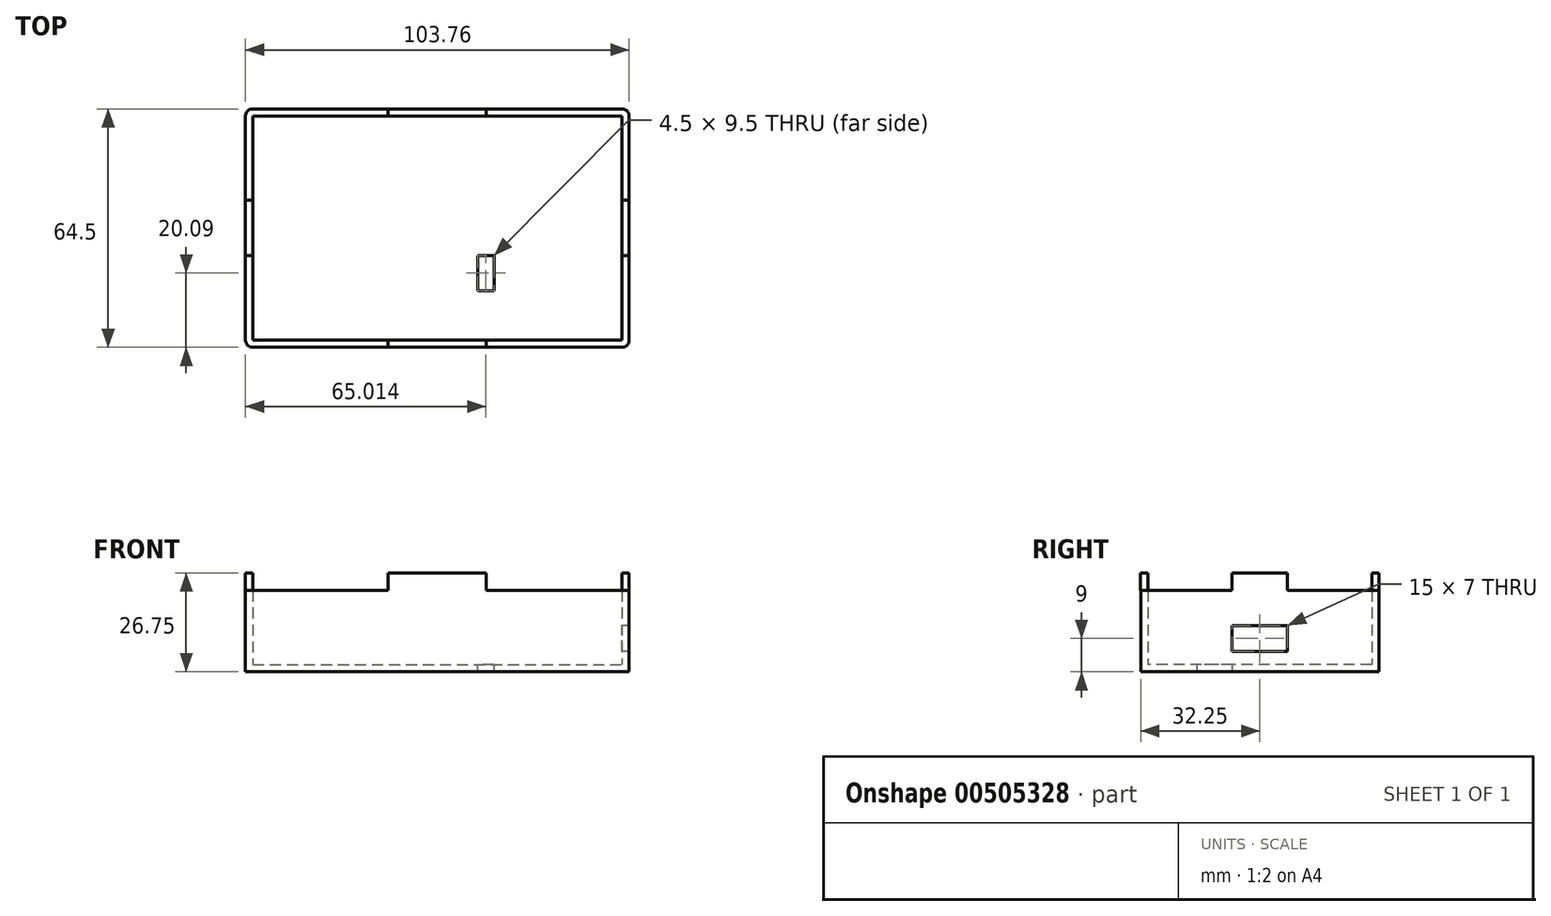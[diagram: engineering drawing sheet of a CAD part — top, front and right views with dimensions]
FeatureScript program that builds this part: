
annotation { "Feature Type Name" : "Feature", "Feature Type Description" : "" }
export const myFeature = defineFeature(function(context is Context, id is Id, definition is map)
    precondition{}
    {
        {
            var Q0;
            Q0=qCreatedBy(makeId("Top.planeOp"),FACE);
            var sketch = newSketch(context, id + "F0", { "sketchPlane" : qUnion([Q0])});
            skLineSegment(sketch, "E0.bottom", {"start": v(-51.88, 32.25) * mm, "end": v(51.88, 32.25) * mm});
            skLineSegment(sketch, "E0.top", {"start": v(-51.88, -32.25) * mm, "end": v(51.88, -32.25) * mm});
            skLineSegment(sketch, "E0.left", {"start": v(-51.88, 32.25) * mm, "end": v(-51.88, -32.25) * mm});
            skLineSegment(sketch, "E0.right", {"start": v(51.88, 32.25) * mm, "end": v(51.88, -32.25) * mm});
            skPoint(sketch, "E0.middle", {"position": v(0, 0) * mm});
            skPoint(sketch, "E1", {"position": v(-51.88, 0) * mm});
            skSolve(sketch);
        }
        {
            var Q0;
            Q0=makeQuery(id+"F0.imprint","IMPRINT",FACE,{"disambiguationData":[TD([[makeQuery(id+"F0.imprint","IMPRINT",EDGE,{"derivedFrom":sQuery(id+"F0.wireOp",EDGE,"E0.bottom")}),-1.0]])]});
            extrude(context, id + "F1", {"entities" : qUnion([Q0]), "depth" : 22 * mm});
        }
        {
            var Q0;
            Q0=makeQuery(id+"F1.opExtrude","CAP_FACE",FACE,{"disambiguationData":[OSD([sQuery(id+"F0.wireOp",EDGE,"E0.bottom"),sQuery(id+"F0.wireOp",EDGE,"E0.top"),sQuery(id+"F0.wireOp",EDGE,"E0.left"),sQuery(id+"F0.wireOp",EDGE,"E0.right")])],"isStart":false});
            shell(context, id + "F2", {"entities" : qUnion([Q0]), "thickness" : 2 * mm});
        }
        {
            var Q0;
            Q0=qCreatedBy(makeId("Top.planeOp"),FACE);
            var sketch = newSketch(context, id + "F3", { "sketchPlane" : qUnion([Q0])});
            skLineSegment(sketch, "E2.bottom", {"start": v(-13.25, 30.25) * mm, "end": v(13.25, 30.25) * mm});
            skLineSegment(sketch, "E2.top", {"start": v(-13.25, 32.25) * mm, "end": v(13.25, 32.25) * mm});
            skLineSegment(sketch, "E2.left", {"start": v(-13.25, 30.25) * mm, "end": v(-13.25, 32.25) * mm});
            skLineSegment(sketch, "E2.right", {"start": v(13.25, 30.25) * mm, "end": v(13.25, 32.25) * mm});
            skSolve(sketch);
        }
        {
            var Q0;
            Q0 = qSketchRegion(id + "F3", true);
            extrude(context, id + "F4", {"entities" : qUnion([Q0]), "operationType" : NewBodyOperationType.ADD, "depth" : 26.75 * mm});
        }
        {
            var Q0;
            Q0=qCreatedBy(makeId("Top.planeOp"),FACE);
            var sketch = newSketch(context, id + "F5", { "sketchPlane" : qUnion([Q0])});
            skLineSegment(sketch, "E3.bottom", {"start": v(-13.25, -32.25) * mm, "end": v(13.25, -32.25) * mm});
            skLineSegment(sketch, "E3.top", {"start": v(-13.25, -30.25) * mm, "end": v(13.25, -30.25) * mm});
            skLineSegment(sketch, "E3.left", {"start": v(-13.25, -32.25) * mm, "end": v(-13.25, -30.25) * mm});
            skLineSegment(sketch, "E3.right", {"start": v(13.25, -32.25) * mm, "end": v(13.25, -30.25) * mm});
            skSolve(sketch);
        }
        {
            var Q0;
            Q0 = qSketchRegion(id + "F5", true);
            extrude(context, id + "F6", {"entities" : qUnion([Q0]), "operationType" : NewBodyOperationType.ADD, "depth" : 26.75 * mm});
        }
        {
            var Q0;
            Q0=qCreatedBy(makeId("Top.planeOp"),FACE);
            var sketch = newSketch(context, id + "F7", { "sketchPlane" : qUnion([Q0])});
            skLineSegment(sketch, "E4.bottom", {"start": v(-51.87, -7.5) * mm, "end": v(-49.87, -7.5) * mm});
            skLineSegment(sketch, "E4.top", {"start": v(-51.87, 7.5) * mm, "end": v(-49.87, 7.5) * mm});
            skLineSegment(sketch, "E4.left", {"start": v(-51.87, -7.5) * mm, "end": v(-51.87, 7.5) * mm});
            skLineSegment(sketch, "E4.right", {"start": v(-49.87, -7.5) * mm, "end": v(-49.87, 7.5) * mm});
            skSolve(sketch);
        }
        {
            var Q0;
            Q0 = qSketchRegion(id + "F7", true);
            extrude(context, id + "F8", {"entities" : qUnion([Q0]), "operationType" : NewBodyOperationType.ADD, "depth" : 26.75 * mm});
        }
        {
            var Q0;
            Q0=qCreatedBy(makeId("Top.planeOp"),FACE);
            var sketch = newSketch(context, id + "F9", { "sketchPlane" : qUnion([Q0])});
            skLineSegment(sketch, "E5.bottom", {"start": v(49.88, -7.5) * mm, "end": v(51.88, -7.5) * mm});
            skLineSegment(sketch, "E5.top", {"start": v(49.88, 7.5) * mm, "end": v(51.88, 7.5) * mm});
            skLineSegment(sketch, "E5.left", {"start": v(49.88, -7.5) * mm, "end": v(49.88, 7.5) * mm});
            skLineSegment(sketch, "E5.right", {"start": v(51.88, -7.5) * mm, "end": v(51.88, 7.5) * mm});
            skSolve(sketch);
        }
        {
            var Q0;
            Q0 = qSketchRegion(id + "F9", true);
            extrude(context, id + "F10", {"entities" : qUnion([Q0]), "operationType" : NewBodyOperationType.ADD, "depth" : 26.75 * mm});
        }
        {
            var Q0;
            Q0=qCreatedBy(makeId("Right.planeOp"),FACE);
            var sketch = newSketch(context, id + "F11", { "sketchPlane" : qUnion([Q0])});
            skLineSegment(sketch, "E6.bottom", {"start": v(7.5, 12.5) * mm, "end": v(-7.5, 12.5) * mm});
            skLineSegment(sketch, "E6.top", {"start": v(7.5, 5.5) * mm, "end": v(-7.5, 5.5) * mm});
            skLineSegment(sketch, "E6.left", {"start": v(7.5, 12.5) * mm, "end": v(7.5, 5.5) * mm});
            skLineSegment(sketch, "E6.right", {"start": v(-7.5, 12.5) * mm, "end": v(-7.5, 5.5) * mm});
            skPoint(sketch, "E7", {"position": v(7.5, 9) * mm});
            skPoint(sketch, "E8", {"position": v(0, 5.5) * mm});
            skSolve(sketch);
        }
        {
            var Q0;
            Q0 = qSketchRegion(id + "F11", true);
            extrude(context, id + "F12", {"entities" : qUnion([Q0]), "operationType" : NewBodyOperationType.REMOVE, "depth" : 381 * mm});
        }
        {
            var Q0;
            Q0=makeQuery(id+"F1.opExtrude","SWEPT_EDGE",EDGE,{"disambiguationData":[OSD([sQuery(id+"F0.wireOp",EDGE,"E0.bottom"),sQuery(id+"F0.wireOp",EDGE,"E0.left")])]});
            var Q1;
            Q1=makeQuery(id+"F1.opExtrude","SWEPT_EDGE",EDGE,{"disambiguationData":[OSD([sQuery(id+"F0.wireOp",EDGE,"E0.top"),sQuery(id+"F0.wireOp",EDGE,"E0.left")])]});
            var Q2;
            Q2=makeQuery(id+"F1.opExtrude","SWEPT_EDGE",EDGE,{"disambiguationData":[OSD([sQuery(id+"F0.wireOp",EDGE,"E0.top"),sQuery(id+"F0.wireOp",EDGE,"E0.right")])]});
            var Q3;
            Q3=makeQuery(id+"F1.opExtrude","SWEPT_EDGE",EDGE,{"disambiguationData":[OSD([sQuery(id+"F0.wireOp",EDGE,"E0.bottom"),sQuery(id+"F0.wireOp",EDGE,"E0.right")])]});
            fillet(context, id + "F13", {"entities" : qUnion([Q0, Q1, Q2, Q3]), "radius" : 2 * mm, "tangentPropagation" : true, "allowEdgeOverflow" : false});
        }
        {
            var Q0;
            Q0=qCreatedBy(makeId("Top.planeOp"),FACE);
            var sketch = newSketch(context, id + "F14", { "sketchPlane" : qUnion([Q0])});
            skPoint(sketch, "E9", {"position": v(-49.87, 0) * mm});
            skLineSegment(sketch, "E10.bottom", {"start": v(15.38, -7.4) * mm, "end": v(10.88, -7.4) * mm});
            skLineSegment(sketch, "E10.top", {"start": v(15.38, -16.9) * mm, "end": v(10.88, -16.9) * mm});
            skLineSegment(sketch, "E10.left", {"start": v(15.38, -7.4) * mm, "end": v(15.38, -16.9) * mm});
            skLineSegment(sketch, "E10.right", {"start": v(10.88, -7.4) * mm, "end": v(10.88, -16.91) * mm});
            skSolve(sketch);
        }
        {
            var Q0;
            Q0 = qSketchRegion(id + "F14", true);
            extrude(context, id + "F15", {"entities" : qUnion([Q0]), "operationType" : NewBodyOperationType.REMOVE, "endBound" : BoundingType.SYMMETRIC, "oppositeDirection" : true, "depth" : 25.4 * mm});
        }
    });
